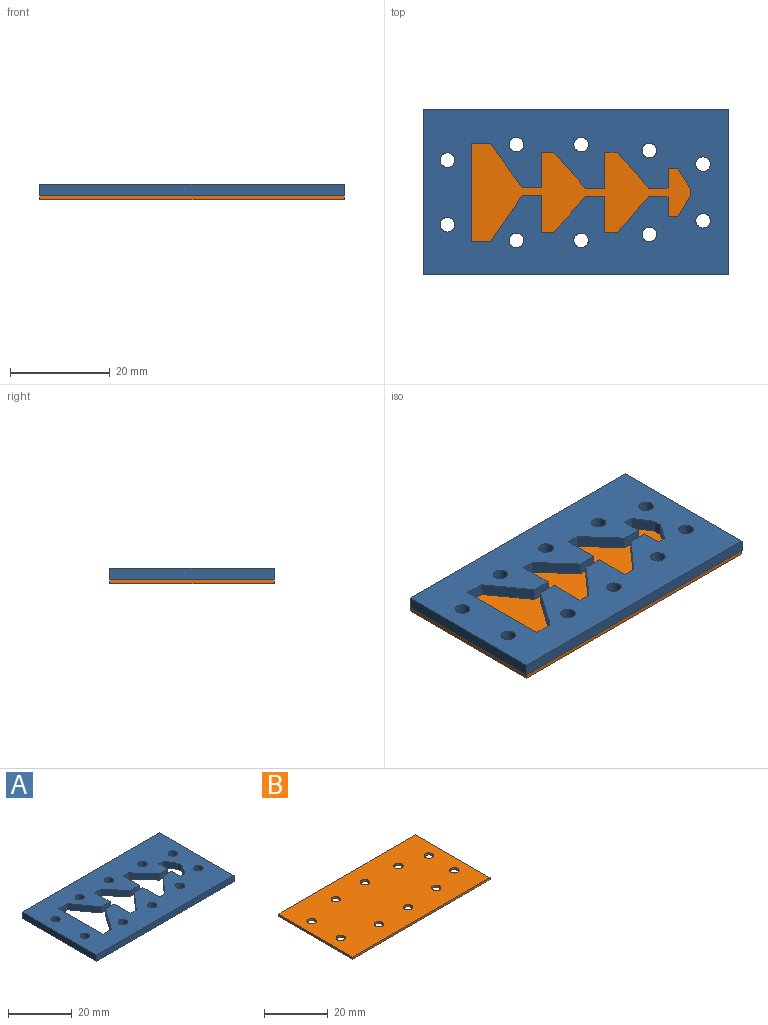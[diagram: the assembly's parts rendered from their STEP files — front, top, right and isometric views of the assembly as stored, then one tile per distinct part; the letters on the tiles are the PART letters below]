
ASSEMBLY  parts=2 mates=1
PART A: 46 faces, bbox 61x33x2.4 mm
  f0: plane 8.79x6.35mm, normal (-0.81,-0.59,0), area 25.8mm2, adj f1,f43,f44,f45
  f1: plane 3.81x2.38mm, normal (0,-1,0), area 9.1mm2, adj f0,f2,f44,f45
  f2: plane 7.01x2.38mm, normal (1,0,0), area 16.7mm2, adj f1,f3,f44,f45
  f3: plane 2.54x2.38mm, normal (0,-1,0), area 6mm2, adj f2,f4,f44,f45
  f4: plane 7.14x6.35mm, normal (-0.75,-0.66,0), area 22.7mm2, adj f3,f5,f44,f45
  f5: plane 3.81x2.38mm, normal (0,-1,0), area 9.1mm2, adj f4,f6,f44,f45
  f6: plane 7.14x2.38mm, normal (1,0,0), area 17mm2, adj f5,f7,f44,f45
  f7: plane 2.54x2.38mm, normal (0,-1,0), area 6mm2, adj f6,f8,f44,f45
  f8: plane 7.14x6.35mm, normal (-0.75,-0.66,0), area 22.7mm2, adj f7,f9,f44,f45
  f9: plane 3.81x2.38mm, normal (0,-1,0), area 9.1mm2, adj f8,f10,f44,f45
  f10: plane 3.96x2.38mm, normal (1,0,0), area 9.4mm2, adj f9,f11,f44,f45
  f11: plane 2.38x1.91mm, normal (0,-1,0), area 4.5mm2, adj f10,f12,f44,f45
  f12: plane 3.98x2.54mm, normal (-0.84,-0.54,0), area 11.2mm2, adj f11,f13,f44,f45
  f13: plane 2.38x1.69mm, normal (-1,0,0), area 4mm2, adj f12,f14,f44,f45
  f14: plane 3.98x2.54mm, normal (-0.84,0.54,0), area 11.2mm2, adj f13,f15,f44,f45
  f15: plane 2.38x1.91mm, normal (0,1,0), area 4.5mm2, adj f14,f16,f44,f45
  f16: plane 4x2.38mm, normal (1,0,0), area 9.5mm2, adj f15,f17,f44,f45
  f17: plane 3.81x2.38mm, normal (0,1,0), area 9.1mm2, adj f16,f18,f44,f45
  f18: plane 7.17x6.35mm, normal (-0.75,0.66,0), area 22.8mm2, adj f17,f19,f44,f45
  f19: plane 2.54x2.38mm, normal (0,1,0), area 6mm2, adj f18,f20,f44,f45
  f20: plane 7.17x2.38mm, normal (1,0,0), area 17.1mm2, adj f19,f21,f44,f45
  f21: plane 3.81x2.38mm, normal (0,1,0), area 9.1mm2, adj f20,f22,f44,f45
  f22: plane 7.17x6.35mm, normal (-0.75,0.66,0), area 22.8mm2, adj f21,f23,f44,f45
  f23: plane 2.54x2.38mm, normal (0,1,0), area 6mm2, adj f22,f24,f44,f45
  f24: plane 7.3x2.38mm, normal (1,0,0), area 17.4mm2, adj f23,f25,f44,f45
  f25: plane 3.81x2.38mm, normal (0,1,0), area 9.1mm2, adj f24,f26,f44,f45
  f26: plane 9.08x6.35mm, normal (-0.82,0.57,0), area 26.4mm2, adj f25,f27,f44,f45
  f27: plane 3.81x2.38mm, normal (0,1,0), area 9.1mm2, adj f26,f28,f44,f45
  f28: plane 19.56x2.38mm, normal (1,0,0), area 46.6mm2, adj f27,f43,f44,f45
  f29: plane 60.96x2.38mm, normal (0,1,0), area 145.2mm2, adj f30,f32,f44,f45
  f30: plane 33.02x2.38mm, normal (-1,0,0), area 78.6mm2, adj f29,f31,f44,f45
  f31: plane 60.96x2.38mm, normal (0,-1,0), area 145.2mm2, adj f30,f32,f44,f45
  f32: plane 33.02x2.38mm, normal (1,0,0), area 78.6mm2, adj f29,f31,f44,f45
  f33: cylinder r=1.46mm len=2.92mm, axis (0,0,1), area 21.9mm2, adj f44,f45
  f34: cylinder r=1.46mm len=2.92mm, axis (0,0,1), area 21.9mm2, adj f44,f45
  f35: cylinder r=1.46mm len=2.92mm, axis (0,0,1), area 21.9mm2, adj f44,f45
  f36: cylinder r=1.46mm len=2.92mm, axis (0,0,1), area 21.9mm2, adj f44,f45
  f37: cylinder r=1.46mm len=2.92mm, axis (0,0,1), area 21.9mm2, adj f44,f45
  f38: cylinder r=1.46mm len=2.92mm, axis (0,0,1), area 21.9mm2, adj f44,f45
  f39: cylinder r=1.46mm len=2.92mm, axis (0,0,1), area 21.9mm2, adj f44,f45
  f40: cylinder r=1.46mm len=2.92mm, axis (0,0,1), area 21.9mm2, adj f44,f45
  f41: cylinder r=1.46mm len=2.92mm, axis (0,0,1), area 21.9mm2, adj f44,f45
  f42: cylinder r=1.46mm len=2.92mm, axis (0,0,1), area 21.9mm2, adj f44,f45
  f43: plane 3.81x2.38mm, normal (0,-1,0), area 9.1mm2, adj f0,f28,f44,f45
  f44: plane 60.96x33.02mm, normal (0,0,-1), area 1558.1mm2, adj f0,f1,f2,f3,f4,f5,f6,f7
  f45: plane 60.96x33.02mm, normal (0,0,1), area 1558.1mm2, adj f0,f1,f2,f3,f4,f5,f6,f7
PART B: 16 faces, bbox 61x33x0.8 mm
  f0: plane 33.02x0.79mm, normal (-1,0,0), area 26.2mm2, adj f1,f13,f14,f15
  f1: plane 60.96x0.79mm, normal (0,-1,0), area 48.4mm2, adj f0,f2,f14,f15
  f2: plane 33.02x0.79mm, normal (1,0,0), area 26.2mm2, adj f1,f13,f14,f15
  f3: cylinder r=1.46mm len=2.92mm, axis (0,0,-1), area 7.3mm2, adj f14,f15
  f4: cylinder r=1.46mm len=2.92mm, axis (0,0,-1), area 7.3mm2, adj f14,f15
  f5: cylinder r=1.46mm len=2.92mm, axis (0,0,-1), area 7.3mm2, adj f14,f15
  f6: cylinder r=1.46mm len=2.92mm, axis (0,0,-1), area 7.3mm2, adj f14,f15
  f7: cylinder r=1.46mm len=2.92mm, axis (0,0,-1), area 7.3mm2, adj f14,f15
  f8: cylinder r=1.46mm len=2.92mm, axis (0,0,-1), area 7.3mm2, adj f14,f15
  f9: cylinder r=1.46mm len=2.92mm, axis (0,0,-1), area 7.3mm2, adj f14,f15
  f10: cylinder r=1.46mm len=2.92mm, axis (0,0,-1), area 7.3mm2, adj f14,f15
  f11: cylinder r=1.46mm len=2.92mm, axis (0,0,-1), area 7.3mm2, adj f14,f15
  f12: cylinder r=1.46mm len=2.92mm, axis (0,0,-1), area 7.3mm2, adj f14,f15
  f13: plane 60.96x0.79mm, normal (0,1,0), area 48.4mm2, adj f0,f2,f14,f15
  f14: plane 60.96x33.02mm, normal (0,0,1), area 1945.9mm2, adj f0,f1,f2,f3,f4,f5,f6,f7
  f15: plane 60.96x33.02mm, normal (0,0,-1), area 1945.9mm2, adj f0,f1,f2,f3,f4,f5,f6,f7
PLACE A t=(43.08,12.86,-34.29)mm
PLACE B t=(85.33,-2.9,-37.46)mm
MATE fastened A.f44 <-> B.f14  axis (0,0,-1) through (65.34,1.05,-36.67)mm
